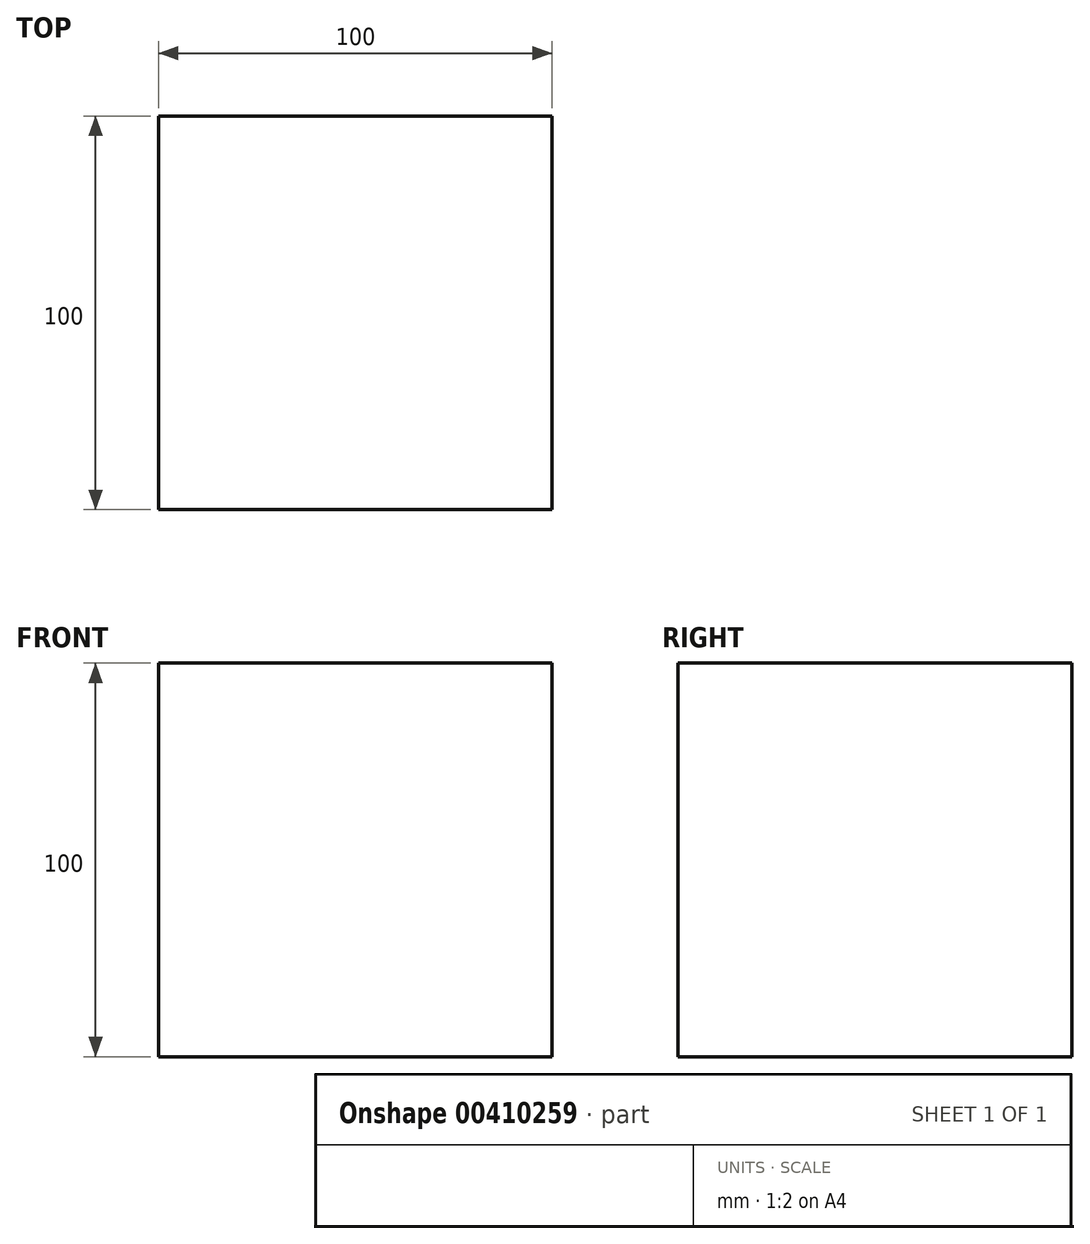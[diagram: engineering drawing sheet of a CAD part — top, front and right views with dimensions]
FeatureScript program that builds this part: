
annotation { "Feature Type Name" : "Feature", "Feature Type Description" : "" }
export const myFeature = defineFeature(function(context is Context, id is Id, definition is map)
    precondition{}
    {
        {
            var Q0;
            Q0=qCreatedBy(makeId("Top.planeOp"),FACE);
            var sketch = newSketch(context, id + "F0", { "sketchPlane" : qUnion([Q0])});
            skLineSegment(sketch, "E0.bottom", {"start": v(50, 50) * mm, "end": v(-50, 50) * mm});
            skLineSegment(sketch, "E0.top", {"start": v(50, -50) * mm, "end": v(-50, -50) * mm});
            skLineSegment(sketch, "E0.left", {"start": v(50, 50) * mm, "end": v(50, -50) * mm});
            skLineSegment(sketch, "E0.right", {"start": v(-50, 50) * mm, "end": v(-50, -50) * mm});
            skPoint(sketch, "E0.middle", {"position": v(0, 0) * mm});
            skSolve(sketch);
        }
        {
            var Q0;
            Q0 = qSketchRegion(id + "F0", true);
            extrude(context, id + "F1", {"entities" : qUnion([Q0]), "depth" : 100 * mm});
        }
    });
